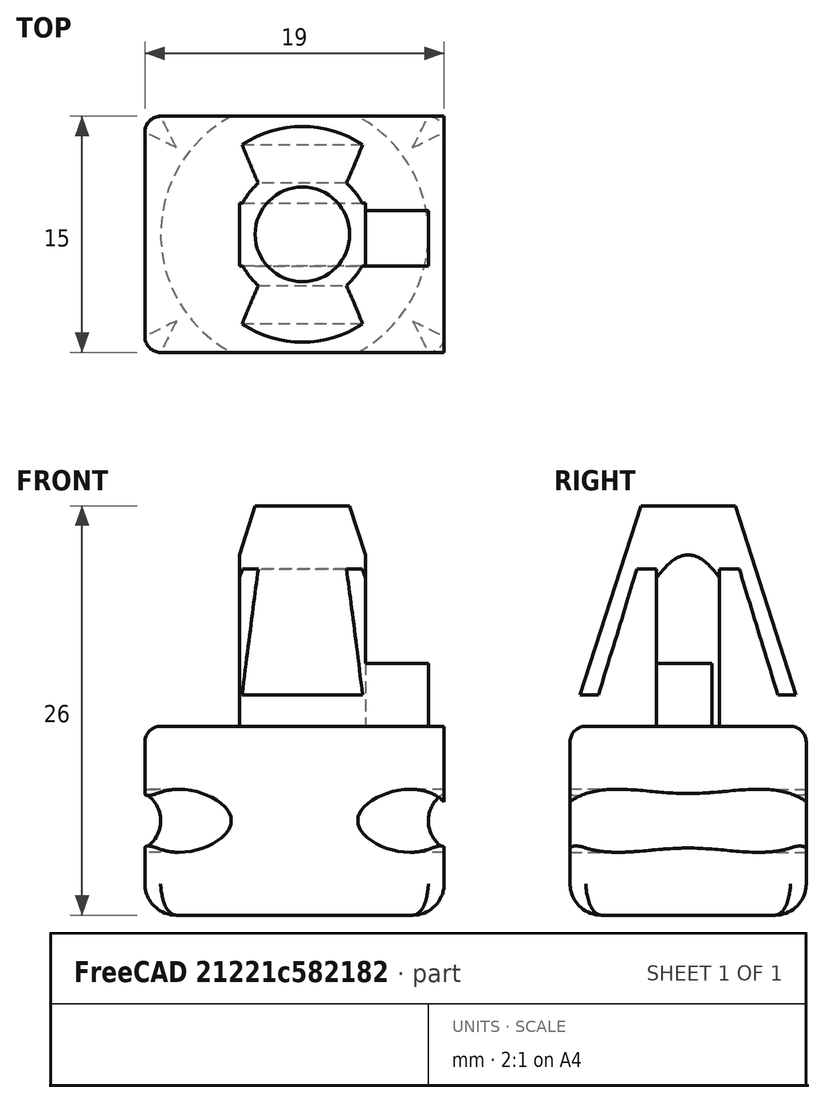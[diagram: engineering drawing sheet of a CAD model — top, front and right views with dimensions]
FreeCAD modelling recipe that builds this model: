
FCSTD DOCUMENT  (FreeCAD 0.14R2935 (Git))
Label: Soporte_maletero_corsa_redondeado
License: CC-BY 3.0
LicenseURL: http://creativecommons.org/licenses/by/3.0/
objects: Part::Box×10, Part::Cut×9, Part::Fillet×6, Part::Cone×1, Part::Torus×1, Part::MultiFuse×1
note: 28 computed .brp shape members not serialized (recipe doc carries the construction recipe); baked Part::Feature solids carry a one-line shape summary decoded from their .brp

FEATURE [Part::Cone] Cone
  Angle = 360
  Height = 14
  Radius1 = 7.5
  Radius2 = 3
FEATURE [Part::Box] Box
  Height = 10
  Length = 20
  Placement = pos=(0,12,0) rot=(0,0,1;0rad)
  Width = 5
FEATURE [Part::Box] Box001
  Height = 18
  Length = 20
  Placement = pos=(0,17.17,-2.83) rot=(1,0,0;0.296705rad)
  Width = 8
FEATURE [Part::Cut] Cut  label="Cuña"
  Base = -> Box
  Placement = pos=(-10,-10,0) rot=(0,0,1;0rad)
  Tool = -> Box001
FEATURE [Part::Box] Box002
  Height = 18
  Length = 20
  Placement = pos=(0,17.17,-2.83) rot=(1,0,0;0.296705rad)
  Width = 8
FEATURE [Part::Box] Box003
  Height = 10
  Length = 20
  Placement = pos=(0,12,0) rot=(0,0,1;0rad)
  Width = 5
FEATURE [Part::Cut] Cut001  label="Cuña001"
  Base = -> Box003
  Placement = pos=(10,10,0) rot=(0,0,1;3.14159rad)
  Tool = -> Box002
FEATURE [Part::Cut] Cut002
  Base = -> Cone
  Tool = -> Cut
FEATURE [Part::Cut] Cut003
  Base = -> Cut002
  Tool = -> Cut001
FEATURE [Part::Box] Box004
  Height = 4
  Length = 11
  Placement = pos=(-3,-2,0) rot=(0,0,1;0rad)
  Width = 3.5
FEATURE [Part::Box] Box005
  Height = 15
  Length = 10
  Placement = pos=(4,-4,0) rot=(0,0,1;0rad)
  Width = 10
FEATURE [Part::Box] Box006
  Height = 15
  Length = 10
  Placement = pos=(-4,-4,0) rot=(0,0,1;1.5708rad)
  Width = 10
FEATURE [Part::Cut] Cut004
  Base = -> Cut003
  Tool = -> Box005
FEATURE [Part::Cut] Cut005
  Base = -> Cut004
  Tool = -> Box006
FEATURE [Part::Box] Box007
  Height = 12
  Length = 19
  Placement = pos=(-10,-7.5,-12) rot=(0,0,1;0rad)
  Width = 15
FEATURE [Part::Box] Box008
  Height = 5
  Length = 10
  Placement = pos=(-5,5,-3) rot=(0,0,1;0rad)
  Width = 10
FEATURE [Part::Box] Box009
  Height = 5
  Length = 10
  Placement = pos=(5,-4,-3) rot=(0,0,1;3.14159rad)
  Width = 10
FEATURE [Part::Cut] Cut006
  Base = -> Cut005
  Tool = -> Box009
FEATURE [Part::Cut] Cut007
  Base = -> Cut006
  Tool = -> Box008
FEATURE [Part::Torus] Torus
  Angle1 = -180
  Angle2 = 180
  Angle3 = 360
  Placement = pos=(-0.5,0,-6) rot=(0,0,1;0rad)
  Radius1 = 10.5
  Radius2 = 2
FEATURE [Part::Cut] Cut008
  Base = -> Box007
  Tool = -> Torus
FEATURE [Part::MultiFuse] Fusion
  Shapes = -> [Box004,Cut007,Cut008]
FEATURE [Part::Fillet] Fillet
  Base = -> Fusion
  Edges = 4 edges r=2: [Edge56,Edge62,Edge72,Edge74]
FEATURE [Part::Fillet] Fillet001
  Base = -> Fillet
  Edges = 1 edges r=1: [Edge27]
FEATURE [Part::Fillet] Fillet002
  Base = -> Fillet001
  Edges = 1 edges r=1: [Edge19]
FEATURE [Part::Fillet] Fillet003
  Base = -> Fillet002
  Edges = 1 edges r=1: [Edge8]
FEATURE [Part::Fillet] Fillet004
  Base = -> Fillet003
  Edges = 1 edges r=1: [Edge54]
FEATURE [Part::Fillet] Fillet005
  Base = -> Fillet004
  Edges = 3 edges r=1: [Edge6,Edge25,Edge36]
